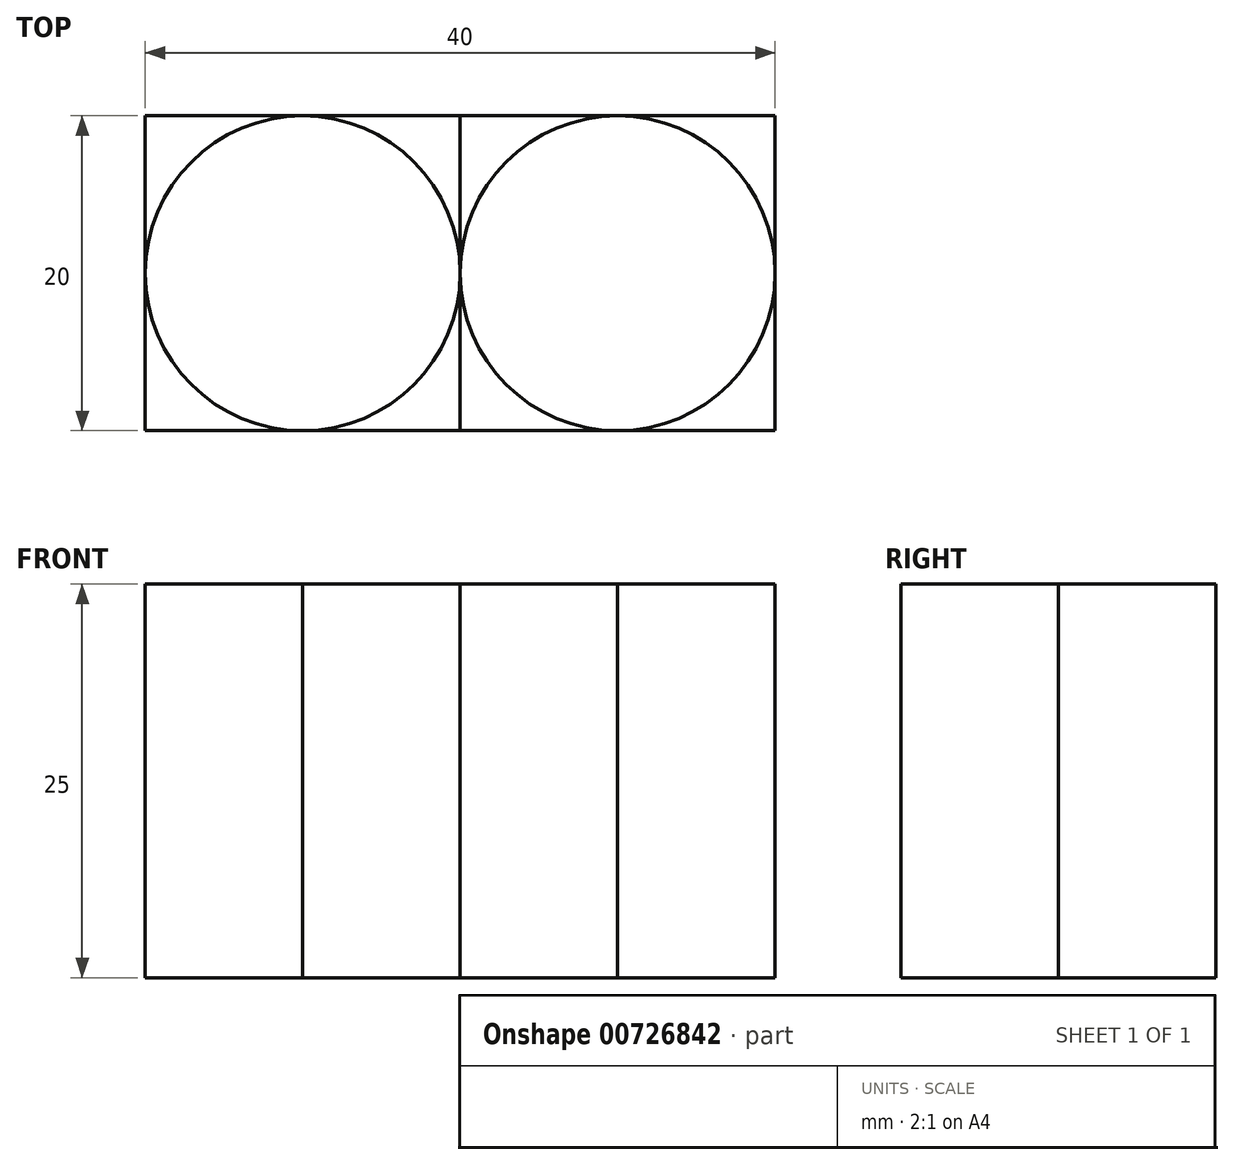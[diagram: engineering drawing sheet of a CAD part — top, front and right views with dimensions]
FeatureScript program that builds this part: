
annotation { "Feature Type Name" : "Feature", "Feature Type Description" : "" }
export const myFeature = defineFeature(function(context is Context, id is Id, definition is map)
    precondition{}
    {
        {
            var Q0;
            Q0=qCreatedBy(makeId("Top.planeOp"),FACE);
            var sketch = newSketch(context, id + "F0", { "sketchPlane" : qUnion([Q0])});
            skLineSegment(sketch, "E0.bottom", {"start": v(-70.18, 13.65) * mm, "end": v(-50.18, 13.65) * mm});
            skLineSegment(sketch, "E0.top", {"start": v(-70.18, -6.35) * mm, "end": v(-50.18, -6.35) * mm});
            skLineSegment(sketch, "E0.left", {"start": v(-70.18, 13.65) * mm, "end": v(-70.18, -6.35) * mm});
            skLineSegment(sketch, "E0.right", {"start": v(-50.18, 13.65) * mm, "end": v(-50.18, -6.35) * mm});
            skCircle(sketch, "E1", {"center": v(-60.18, 3.65) * mm, "radius": 10 * mm});
            skLineSegment(sketch, "E2.1.0.0", {"start": v(-50.18, -6.35) * mm, "end": v(-30.18, -6.35) * mm});
            skLineSegment(sketch, "E2.1.0.1", {"start": v(-30.18, 13.65) * mm, "end": v(-30.18, -6.35) * mm});
            skLineSegment(sketch, "E2.1.0.3", {"start": v(-50.18, 13.65) * mm, "end": v(-30.18, 13.65) * mm});
            skCircle(sketch, "E2.1.0.4", {"center": v(-40.18, 3.65) * mm, "radius": 10 * mm});
            skLineSegment(sketch, "E2.direction1", {"start": v(-70.18, -6.35) * mm, "end": v(-50.18, -6.35) * mm, "construction": true});
            skSolve(sketch);
        }
        {
            var Q0;
            {var subQ0=sQuery(id+"F0.wireOp",EDGE,"E0.left");var subQ1=sQuery(id+"F0.wireOp",EDGE,"E0.bottom");var subQ2=makeQuery(id+"F0.imprint","INTERSECT",VERTEX,{"derivedFrom":[subQ1,subQ0]});Q0=makeQuery(id+"F0.imprint","IMPRINT",FACE,{"disambiguationData":[TD([[makeQuery(id+"F0.imprint","IMPRINT",EDGE,{"disambiguationData":[TD([[subQ2,-1.0]])],"derivedFrom":subQ1}),-1.0]])]});}
            var Q1;
            {var subQ1=sQuery(id+"F0.wireOp",EDGE,"E0.top");var subQ3=sQuery(id+"F0.wireOp",EDGE,"E1");var subQ4=makeQuery(id+"F0.imprint","INTERSECT",VERTEX,{"derivedFrom":[subQ1,subQ3]});Q1=makeQuery(id+"F0.imprint","IMPRINT",FACE,{"disambiguationData":[TD([[makeQuery(id+"F0.imprint","IMPRINT",EDGE,{"disambiguationData":[TD([[subQ4,-1.0]])],"derivedFrom":subQ1}),1.0]])]});}
            var Q2;
            {var subQ0=sQuery(id+"F0.wireOp",EDGE,"E2.1.0.3");var subQ3=sQuery(id+"F0.wireOp",EDGE,"E2.1.0.4");var subQ5=makeQuery(id+"F0.imprint","INTERSECT",VERTEX,{"derivedFrom":[subQ0,subQ3]});Q2=makeQuery(id+"F0.imprint","IMPRINT",FACE,{"disambiguationData":[TD([[makeQuery(id+"F0.imprint","IMPRINT",EDGE,{"disambiguationData":[TD([[subQ5,1.0]])],"derivedFrom":subQ0}),-1.0]])]});}
            var Q3;
            {var subQ0=sQuery(id+"F0.wireOp",EDGE,"E2.1.0.1");var subQ1=sQuery(id+"F0.wireOp",EDGE,"E2.1.0.0");var subQ2=makeQuery(id+"F0.imprint","INTERSECT",VERTEX,{"derivedFrom":[subQ1,subQ0]});Q3=makeQuery(id+"F0.imprint","IMPRINT",FACE,{"disambiguationData":[TD([[makeQuery(id+"F0.imprint","IMPRINT",EDGE,{"disambiguationData":[TD([[subQ2,1.0]])],"derivedFrom":subQ1}),1.0]])]});}
            extrude(context, id + "F1", {"entities" : qUnion([Q0, Q1, Q2, Q3]), "depth" : 25 * mm, "offsetDistance" : 25 * mm});
        }
        {
            var Q0;
            {var subQ0=sQuery(id+"F0.wireOp",EDGE,"E0.left");var subQ1=sQuery(id+"F0.wireOp",EDGE,"E0.top");var subQ2=makeQuery(id+"F0.imprint","INTERSECT",VERTEX,{"derivedFrom":[subQ1,subQ0]});Q0=makeQuery(id+"F0.imprint","IMPRINT",FACE,{"disambiguationData":[TD([[makeQuery(id+"F0.imprint","IMPRINT",EDGE,{"disambiguationData":[TD([[subQ2,-1.0]])],"derivedFrom":subQ1}),1.0]])]});}
            var Q1;
            {var subQ1=sQuery(id+"F0.wireOp",EDGE,"E0.bottom");var subQ3=sQuery(id+"F0.wireOp",EDGE,"E1");var subQ4=makeQuery(id+"F0.imprint","INTERSECT",VERTEX,{"derivedFrom":[subQ1,subQ3]});Q1=makeQuery(id+"F0.imprint","IMPRINT",FACE,{"disambiguationData":[TD([[makeQuery(id+"F0.imprint","IMPRINT",EDGE,{"disambiguationData":[TD([[subQ4,-1.0]])],"derivedFrom":subQ1}),-1.0]])]});}
            var Q2;
            {var subQ1=sQuery(id+"F0.wireOp",EDGE,"E2.1.0.0");var subQ3=sQuery(id+"F0.wireOp",EDGE,"E2.1.0.4");var subQ4=makeQuery(id+"F0.imprint","INTERSECT",VERTEX,{"derivedFrom":[subQ1,subQ3]});Q2=makeQuery(id+"F0.imprint","IMPRINT",FACE,{"disambiguationData":[TD([[makeQuery(id+"F0.imprint","IMPRINT",EDGE,{"disambiguationData":[TD([[subQ4,1.0]])],"derivedFrom":subQ1}),1.0]])]});}
            var Q3;
            {var subQ0=sQuery(id+"F0.wireOp",EDGE,"E2.1.0.3");var subQ1=sQuery(id+"F0.wireOp",EDGE,"E2.1.0.1");var subQ2=makeQuery(id+"F0.imprint","INTERSECT",VERTEX,{"derivedFrom":[subQ1,subQ0]});Q3=makeQuery(id+"F0.imprint","IMPRINT",FACE,{"disambiguationData":[TD([[makeQuery(id+"F0.imprint","IMPRINT",EDGE,{"disambiguationData":[TD([[subQ2,-1.0]])],"derivedFrom":subQ1}),-1.0]])]});}
            extrude(context, id + "F2", {"entities" : qUnion([Q0, Q1, Q2, Q3]), "depth" : 25 * mm, "offsetDistance" : 25 * mm});
        }
        {
            var Q0;
            {var subQ0=sQuery(id+"F0.wireOp",EDGE,"E1");var subQ1=makeQuery(id+"F0.imprint","INTERSECT",VERTEX,{"derivedFrom":[sQuery(id+"F0.wireOp",EDGE,"E0.bottom"),subQ0]});Q0=makeQuery(id+"F0.imprint","IMPRINT",FACE,{"disambiguationData":[TD([[makeQuery(id+"F0.imprint","IMPRINT",EDGE,{"disambiguationData":[TD([[subQ1,-1.0]])],"derivedFrom":subQ0}),1.0]])]});}
            var Q1;
            {var subQ0=sQuery(id+"F0.wireOp",EDGE,"E2.1.0.4");var subQ1=makeQuery(id+"F0.imprint","INTERSECT",VERTEX,{"derivedFrom":[sQuery(id+"F0.wireOp",EDGE,"E2.1.0.1"),subQ0]});Q1=makeQuery(id+"F0.imprint","IMPRINT",FACE,{"disambiguationData":[TD([[makeQuery(id+"F0.imprint","IMPRINT",EDGE,{"disambiguationData":[TD([[subQ1,-1.0]])],"derivedFrom":subQ0}),1.0]])]});}
            extrude(context, id + "F3", {"entities" : qUnion([Q0, Q1]), "depth" : 25 * mm, "offsetDistance" : 25 * mm});
        }
    });
